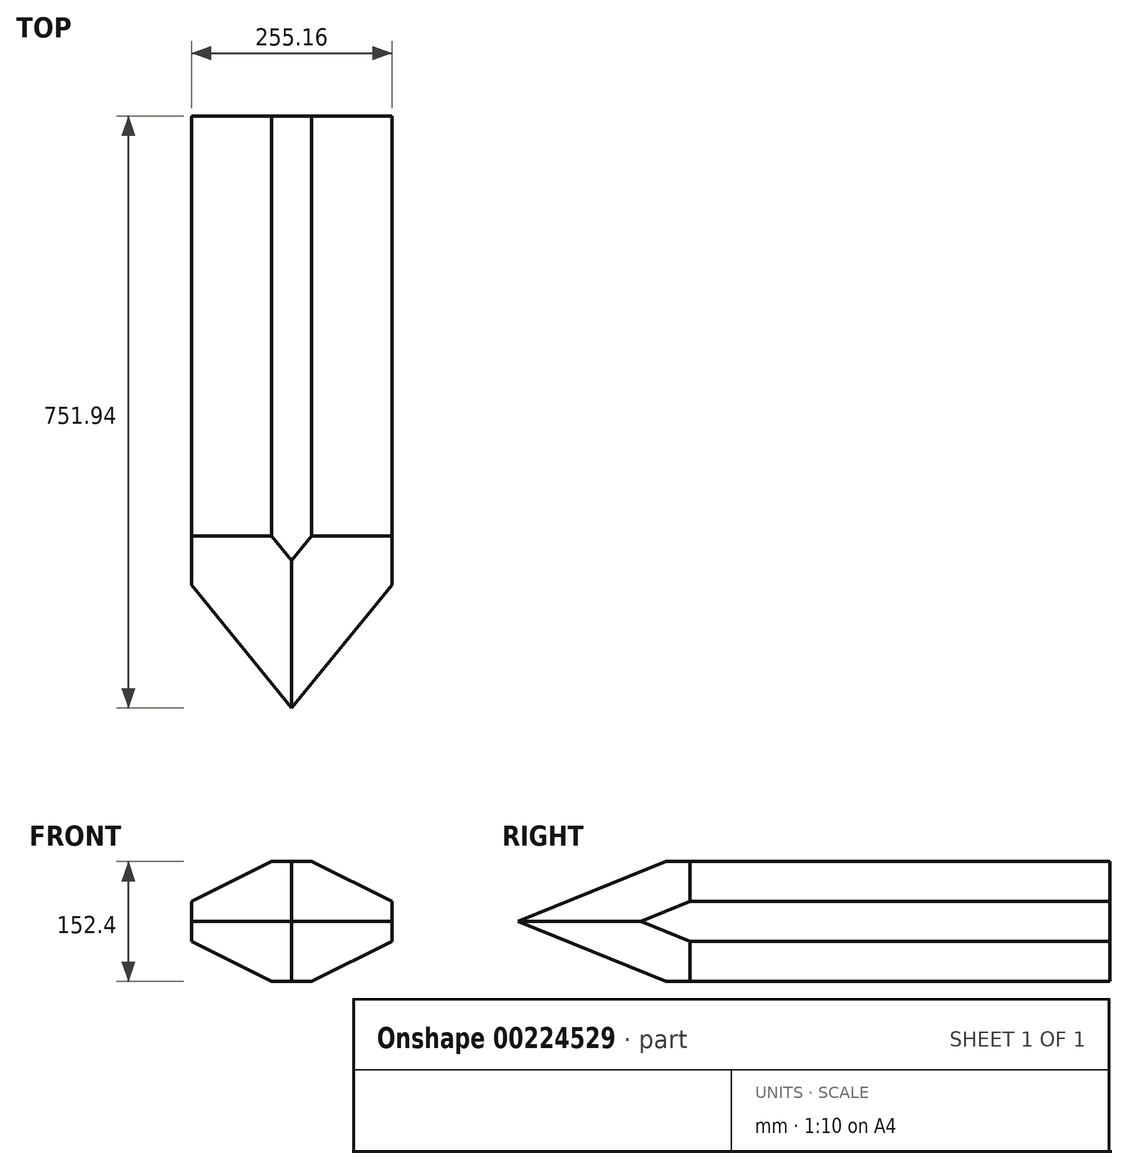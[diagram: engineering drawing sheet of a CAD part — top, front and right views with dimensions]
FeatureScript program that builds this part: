
annotation { "Feature Type Name" : "Feature", "Feature Type Description" : "" }
export const myFeature = defineFeature(function(context is Context, id is Id, definition is map)
    precondition{}
    {
        {
            var Q0;
            Q0=qCreatedBy(makeId("Front.planeOp"),FACE);
            var sketch = newSketch(context, id + "F0", { "sketchPlane" : qUnion([Q0])});
            skLineSegment(sketch, "E0", {"start": v(0, 76.2) * mm, "end": v(-25.4, 76.2) * mm});
            skLineSegment(sketch, "E1.MirrorCS", {"start": v(0, -76.2) * mm, "end": v(-25.4, -76.2) * mm});
            skLineSegment(sketch, "E2", {"start": v(-127.58, 0) * mm, "end": v(-127.58, 25.4) * mm});
            skLineSegment(sketch, "E3", {"start": v(-127.58, 25.4) * mm, "end": v(-25.4, 76.2) * mm});
            skLineSegment(sketch, "E4.MirrorCS", {"start": v(127.58, 25.4) * mm, "end": v(25.4, 76.2) * mm});
            skLineSegment(sketch, "E5.MirrorCS", {"start": v(127.58, 0) * mm, "end": v(127.58, 25.4) * mm});
            skLineSegment(sketch, "E6.MirrorCS", {"start": v(0, 76.2) * mm, "end": v(25.4, 76.2) * mm});
            skLineSegment(sketch, "E7.MirrorCS", {"start": v(0, -76.2) * mm, "end": v(25.4, -76.2) * mm});
            skLineSegment(sketch, "E8.MirrorCS", {"start": v(127.58, -25.4) * mm, "end": v(25.4, -76.2) * mm});
            skLineSegment(sketch, "E9.MirrorCS", {"start": v(-127.58, -25.4) * mm, "end": v(-25.4, -76.2) * mm});
            skLineSegment(sketch, "E10.MirrorCS", {"start": v(-127.58, 0) * mm, "end": v(-127.58, -25.4) * mm});
            skLineSegment(sketch, "E11.MirrorCS", {"start": v(127.58, 0) * mm, "end": v(127.58, -25.4) * mm});
            skLineSegment(sketch, "E12", {"start": v(127.58, 0) * mm, "end": v(0, 0) * mm});
            skSolve(sketch);
        }
        {
            var Q0;
            Q0=makeQuery(id+"F0.imprint","IMPRINT",FACE,{"disambiguationData":[TD([[makeQuery(id+"F0.imprint","IMPRINT",EDGE,{"derivedFrom":sQuery(id+"F0.wireOp",EDGE,"E0")}),1.0]])]});
            extrude(context, id + "F1", {"entities" : qUnion([Q0]), "depth" : 762 * mm});
        }
        {
            var Q0;
            Q0=makeQuery(id+"F1.opExtrude","CAP_EDGE",EDGE,{"disambiguationData":[OSD([sQuery(id+"F0.wireOp",EDGE,"E3")])],"isStart":false});
            var Q1;
            Q1=makeQuery(id+"F1.opExtrude","CAP_EDGE",EDGE,{"disambiguationData":[OSD([sQuery(id+"F0.wireOp",EDGE,"E4.MirrorCS")])],"isStart":false});
            var Q2;
            Q2=makeQuery(id+"F1.opExtrude","CAP_EDGE",EDGE,{"disambiguationData":[OSD([sQuery(id+"F0.wireOp",EDGE,"E8.MirrorCS")])],"isStart":false});
            var Q3;
            Q3=makeQuery(id+"F1.opExtrude","CAP_EDGE",EDGE,{"disambiguationData":[OSD([sQuery(id+"F0.wireOp",EDGE,"E9.MirrorCS")])],"isStart":false});
            chamfer(context, id + "F2", {"entities" : qUnion([Q0, Q1, Q2, Q3]), "chamferType" : ChamferType.OFFSET_ANGLE, "width" : 228.6 * mm, "oppositeDirection" : false, "angle" : 20 * degree, "tangentPropagation" : true});
        }
    });
